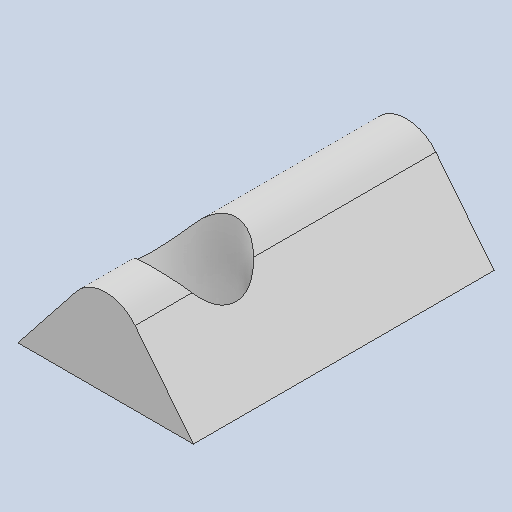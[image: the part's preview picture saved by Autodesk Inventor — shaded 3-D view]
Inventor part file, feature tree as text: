
AUTODESK INVENTOR PART (.ipt)
format: ipt  version: 2022 (Build 260153000, 153)  size: 90,112 bytes
history: native  units: in
note: dims shown in document units (in); Inventor stores cm internally (conversion verified against a paired STEP export)
features: hole x1
ambient origin geometry x8: Origin, YZ Plane, XZ Plane, XY Plane, X Axis, Y Axis, Z Axis, Center Point
bodies: Solid1 (feature_tree)
feature tree (1):
  hole  "Hole1"  [1 undecoded]
note: 1 required parameter value undecoded (feature->parameter linkage not recoverable at this tier; creation-order binding heuristic only, values carry confidence <= 0.55)
